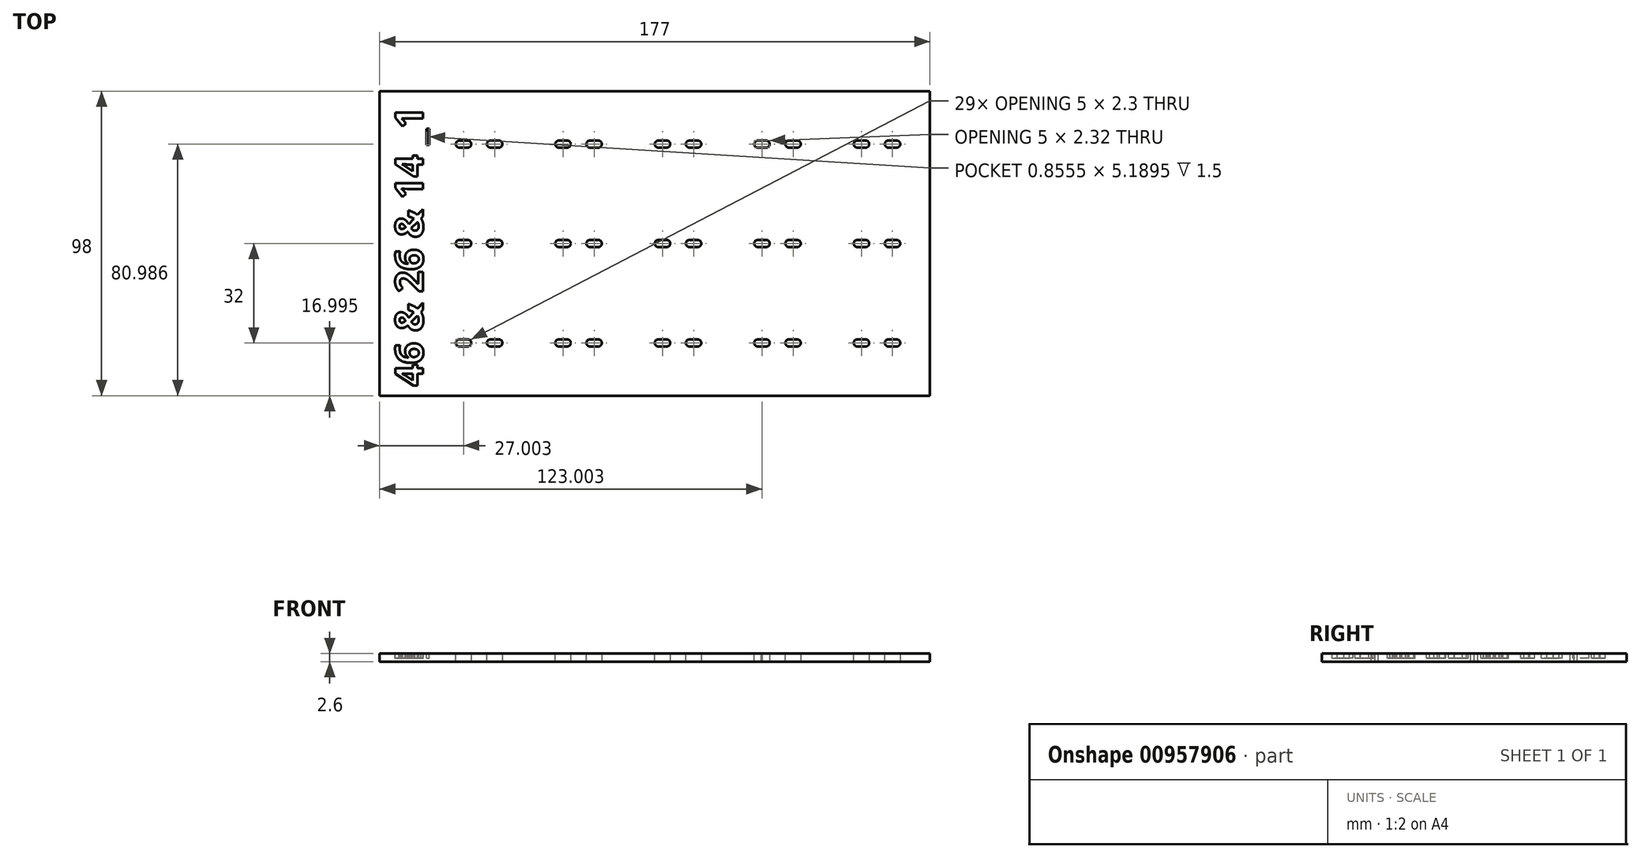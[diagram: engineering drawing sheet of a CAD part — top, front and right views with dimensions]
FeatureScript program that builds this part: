
annotation { "Feature Type Name" : "Feature", "Feature Type Description" : "" }
export const myFeature = defineFeature(function(context is Context, id is Id, definition is map)
    precondition{}
    {
        {
            var Q0;
            Q0=qCreatedBy(makeId("Top.planeOp"),FACE);
            var sketch = newSketch(context, id + "F0", { "sketchPlane" : qUnion([Q0])});
            skLineSegment(sketch, "E0.bottom", {"start": v(-87.55, 48.72) * mm, "end": v(89.45, 48.72) * mm});
            skLineSegment(sketch, "E0.top", {"start": v(-87.55, -49.28) * mm, "end": v(89.45, -49.28) * mm});
            skLineSegment(sketch, "E0.left", {"start": v(-87.55, 48.72) * mm, "end": v(-87.55, -49.28) * mm});
            skLineSegment(sketch, "E0.right", {"start": v(89.45, 48.72) * mm, "end": v(89.45, -49.28) * mm});
            skSolve(sketch);
        }
        {
            var Q0;
            Q0=makeQuery(id+"F0.imprint","IMPRINT",FACE,{"disambiguationData":[TD([[makeQuery(id+"F0.imprint","IMPRINT",EDGE,{"derivedFrom":sQuery(id+"F0.wireOp",EDGE,"E0.bottom")}),-1.0]])]});
            extrude(context, id + "F1", {"entities" : qUnion([Q0]), "depth" : 2.6 * mm, "offsetDistance" : 25 * mm});
        }
        {
            var Q0;
            Q0=makeQuery(id+"F1.opExtrude","CAP_FACE",FACE,{"disambiguationData":[OSD([sQuery(id+"F0.wireOp",EDGE,"E0.bottom"),sQuery(id+"F0.wireOp",EDGE,"E0.top"),sQuery(id+"F0.wireOp",EDGE,"E0.left"),sQuery(id+"F0.wireOp",EDGE,"E0.right")])],"isStart":false});
            var sketch = newSketch(context, id + "F2", { "sketchPlane" : qUnion([Q0])});
            skText(sketch, "E1", { "text": "46 & 26 & 14 _1", "fontName": "OpenSans-Bold.ttf"});
            const initialGuessF2  = {"E1": [-0.07355, -0.04628, 0, 1, 0.009]};
            skSetInitialGuess(sketch, initialGuessF2);
            skSolve(sketch);
        }
        {
            var Q0;
            Q0=qSketchRegion(id+"F2",true);
            extrude(context, id + "F3", {"entities" : qUnion([Q0]), "operationType" : NewBodyOperationType.REMOVE, "oppositeDirection" : true, "depth" : 1.5 * mm, "offsetDistance" : 25 * mm});
        }
        {
            var Q0;
            {var subQ0=sQuery(id+"F0.wireOp",EDGE,"E0.left");var subQ1=sQuery(id+"F0.wireOp",EDGE,"E0.bottom");var subQ2=sQuery(id+"F0.wireOp",EDGE,"E0.right");var subQ3=sQuery(id+"F0.wireOp",EDGE,"E0.top");Q0=makeQuery(id+"F3.boolean.opBoolean","SPLIT",FACE,{"disambiguationData":[TD([makeQuery(id+"F1.opExtrude","SWEPT_FACE",FACE,{"disambiguationData":[OSD([subQ1])]})])],"derivedFrom":makeQuery(id+"F1.opExtrude","CAP_FACE",FACE,{"disambiguationData":[OSD([subQ1,subQ3,subQ0,subQ2])],"isStart":false})});}
            var sketch = newSketch(context, id + "F4", { "sketchPlane" : qUnion([Q0])});
            skCircle(sketch, "E2", {"center": v(-60.55, 31.72) * mm, "radius": 1.15 * mm});
            skCircle(sketch, "E3", {"center": v(-50.55, 31.72) * mm, "radius": 1.15 * mm});
            skCircle(sketch, "E4", {"center": v(-28.55, 31.72) * mm, "radius": 1.15 * mm});
            skCircle(sketch, "E5", {"center": v(-18.55, 31.72) * mm, "radius": 1.15 * mm});
            skCircle(sketch, "E6", {"center": v(3.45, 31.72) * mm, "radius": 1.15 * mm});
            skCircle(sketch, "E7", {"center": v(13.45, 31.72) * mm, "radius": 1.15 * mm});
            skCircle(sketch, "E8", {"center": v(35.45, 31.72) * mm, "radius": 1.15 * mm});
            skCircle(sketch, "E9", {"center": v(45.45, 31.72) * mm, "radius": 1.15 * mm});
            skCircle(sketch, "E10", {"center": v(67.45, 31.72) * mm, "radius": 1.15 * mm});
            skCircle(sketch, "E11", {"center": v(77.45, 31.72) * mm, "radius": 1.15 * mm});
            skCircle(sketch, "E12", {"center": v(-60.55, -0.28) * mm, "radius": 1.15 * mm});
            skCircle(sketch, "E13", {"center": v(-50.55, -0.28) * mm, "radius": 1.15 * mm});
            skCircle(sketch, "E14", {"center": v(-28.55, -0.28) * mm, "radius": 1.15 * mm});
            skCircle(sketch, "E15", {"center": v(-18.55, -0.28) * mm, "radius": 1.15 * mm});
            skCircle(sketch, "E16", {"center": v(3.45, -0.28) * mm, "radius": 1.15 * mm});
            skCircle(sketch, "E17", {"center": v(13.45, -0.28) * mm, "radius": 1.15 * mm});
            skCircle(sketch, "E18", {"center": v(35.45, -0.28) * mm, "radius": 1.15 * mm});
            skCircle(sketch, "E19", {"center": v(45.45, -0.28) * mm, "radius": 1.15 * mm});
            skCircle(sketch, "E20", {"center": v(67.45, -0.28) * mm, "radius": 1.15 * mm});
            skCircle(sketch, "E21", {"center": v(77.45, -0.28) * mm, "radius": 1.15 * mm});
            skCircle(sketch, "E22", {"center": v(-60.55, -32.28) * mm, "radius": 1.15 * mm});
            skCircle(sketch, "E23", {"center": v(-50.55, -32.28) * mm, "radius": 1.15 * mm});
            skCircle(sketch, "E24", {"center": v(-28.55, -32.28) * mm, "radius": 1.15 * mm});
            skCircle(sketch, "E25", {"center": v(-18.55, -32.28) * mm, "radius": 1.15 * mm});
            skCircle(sketch, "E26", {"center": v(3.45, -32.28) * mm, "radius": 1.15 * mm});
            skCircle(sketch, "E27", {"center": v(13.45, -32.28) * mm, "radius": 1.15 * mm});
            skCircle(sketch, "E28", {"center": v(35.45, -32.28) * mm, "radius": 1.15 * mm});
            skCircle(sketch, "E29", {"center": v(45.45, -32.28) * mm, "radius": 1.15 * mm});
            skCircle(sketch, "E30", {"center": v(67.45, -32.28) * mm, "radius": 1.15 * mm});
            skCircle(sketch, "E31", {"center": v(77.45, -32.28) * mm, "radius": 1.15 * mm});
            skLineSegment(sketch, "E32.bottom", {"start": v(-53.05, 32.87) * mm, "end": v(-48.05, 32.87) * mm});
            skLineSegment(sketch, "E32.top", {"start": v(-53.05, 30.57) * mm, "end": v(-48.05, 30.57) * mm});
            skLineSegment(sketch, "E32.left", {"start": v(-53.05, 32.87) * mm, "end": v(-53.05, 30.57) * mm});
            skLineSegment(sketch, "E32.right", {"start": v(-48.05, 32.87) * mm, "end": v(-48.05, 30.57) * mm});
            skLineSegment(sketch, "E33.bottom", {"start": v(-63.05, 32.87) * mm, "end": v(-58.05, 32.87) * mm});
            skLineSegment(sketch, "E33.top", {"start": v(-63.05, 30.57) * mm, "end": v(-58.05, 30.57) * mm});
            skLineSegment(sketch, "E33.left", {"start": v(-63.05, 32.87) * mm, "end": v(-63.05, 30.57) * mm});
            skLineSegment(sketch, "E33.right", {"start": v(-58.05, 32.87) * mm, "end": v(-58.05, 30.57) * mm});
            skLineSegment(sketch, "E34.bottom", {"start": v(-31.05, 32.87) * mm, "end": v(-26.05, 32.87) * mm});
            skLineSegment(sketch, "E34.top", {"start": v(-31.05, 30.57) * mm, "end": v(-26.05, 30.57) * mm});
            skLineSegment(sketch, "E34.left", {"start": v(-31.05, 32.87) * mm, "end": v(-31.05, 30.57) * mm});
            skLineSegment(sketch, "E34.right", {"start": v(-26.05, 32.87) * mm, "end": v(-26.05, 30.57) * mm});
            skLineSegment(sketch, "E35.bottom", {"start": v(-21.05, 32.87) * mm, "end": v(-16.05, 32.87) * mm});
            skLineSegment(sketch, "E35.top", {"start": v(-21.05, 30.57) * mm, "end": v(-16.05, 30.57) * mm});
            skLineSegment(sketch, "E35.left", {"start": v(-21.05, 32.87) * mm, "end": v(-21.05, 30.57) * mm});
            skLineSegment(sketch, "E35.right", {"start": v(-16.05, 32.87) * mm, "end": v(-16.05, 30.57) * mm});
            skLineSegment(sketch, "E36.bottom", {"start": v(0.95, 32.87) * mm, "end": v(5.95, 32.87) * mm});
            skLineSegment(sketch, "E36.top", {"start": v(0.95, 30.57) * mm, "end": v(5.95, 30.57) * mm});
            skLineSegment(sketch, "E36.left", {"start": v(0.95, 32.87) * mm, "end": v(0.95, 30.57) * mm});
            skLineSegment(sketch, "E36.right", {"start": v(5.95, 32.87) * mm, "end": v(5.95, 30.57) * mm});
            skLineSegment(sketch, "E37.bottom", {"start": v(10.95, 32.87) * mm, "end": v(15.95, 32.87) * mm});
            skLineSegment(sketch, "E37.top", {"start": v(10.95, 30.57) * mm, "end": v(15.95, 30.57) * mm});
            skLineSegment(sketch, "E37.left", {"start": v(10.95, 32.87) * mm, "end": v(10.95, 30.57) * mm});
            skLineSegment(sketch, "E37.right", {"start": v(15.95, 32.87) * mm, "end": v(15.95, 30.57) * mm});
            skLineSegment(sketch, "E38.bottom", {"start": v(32.95, 32.85) * mm, "end": v(37.95, 32.85) * mm});
            skLineSegment(sketch, "E38.top", {"start": v(32.95, 30.55) * mm, "end": v(37.95, 30.55) * mm});
            skLineSegment(sketch, "E38.left", {"start": v(32.95, 32.85) * mm, "end": v(32.95, 30.55) * mm});
            skLineSegment(sketch, "E38.right", {"start": v(37.95, 32.85) * mm, "end": v(37.95, 30.55) * mm});
            skLineSegment(sketch, "E39.bottom", {"start": v(42.95, 32.87) * mm, "end": v(47.95, 32.87) * mm});
            skLineSegment(sketch, "E39.top", {"start": v(42.95, 30.57) * mm, "end": v(47.95, 30.57) * mm});
            skLineSegment(sketch, "E39.left", {"start": v(42.95, 32.87) * mm, "end": v(42.95, 30.57) * mm});
            skLineSegment(sketch, "E39.right", {"start": v(47.95, 32.87) * mm, "end": v(47.95, 30.57) * mm});
            skLineSegment(sketch, "E40.bottom", {"start": v(64.95, 32.87) * mm, "end": v(69.95, 32.87) * mm});
            skLineSegment(sketch, "E40.top", {"start": v(64.95, 30.57) * mm, "end": v(69.95, 30.57) * mm});
            skLineSegment(sketch, "E40.left", {"start": v(64.95, 32.87) * mm, "end": v(64.95, 30.57) * mm});
            skLineSegment(sketch, "E40.right", {"start": v(69.95, 32.87) * mm, "end": v(69.95, 30.57) * mm});
            skLineSegment(sketch, "E41.bottom", {"start": v(74.95, 32.87) * mm, "end": v(79.95, 32.87) * mm});
            skLineSegment(sketch, "E41.top", {"start": v(74.95, 30.57) * mm, "end": v(79.95, 30.57) * mm});
            skLineSegment(sketch, "E41.left", {"start": v(74.95, 32.87) * mm, "end": v(74.95, 30.57) * mm});
            skLineSegment(sketch, "E41.right", {"start": v(79.95, 32.87) * mm, "end": v(79.95, 30.57) * mm});
            skLineSegment(sketch, "E42.bottom", {"start": v(74.95, 0.87) * mm, "end": v(79.95, 0.87) * mm});
            skLineSegment(sketch, "E42.top", {"start": v(74.95, -1.43) * mm, "end": v(79.95, -1.43) * mm});
            skLineSegment(sketch, "E42.left", {"start": v(74.95, 0.87) * mm, "end": v(74.95, -1.43) * mm});
            skLineSegment(sketch, "E42.right", {"start": v(79.95, 0.87) * mm, "end": v(79.95, -1.43) * mm});
            skLineSegment(sketch, "E43.bottom", {"start": v(64.95, 0.87) * mm, "end": v(69.95, 0.87) * mm});
            skLineSegment(sketch, "E43.top", {"start": v(64.95, -1.43) * mm, "end": v(69.95, -1.43) * mm});
            skLineSegment(sketch, "E43.left", {"start": v(64.95, 0.87) * mm, "end": v(64.95, -1.43) * mm});
            skLineSegment(sketch, "E43.right", {"start": v(69.95, 0.87) * mm, "end": v(69.95, -1.43) * mm});
            skLineSegment(sketch, "E44.bottom", {"start": v(42.95, 0.87) * mm, "end": v(47.95, 0.87) * mm});
            skLineSegment(sketch, "E44.top", {"start": v(42.95, -1.43) * mm, "end": v(47.95, -1.43) * mm});
            skLineSegment(sketch, "E44.left", {"start": v(42.95, 0.87) * mm, "end": v(42.95, -1.43) * mm});
            skLineSegment(sketch, "E44.right", {"start": v(47.95, 0.87) * mm, "end": v(47.95, -1.43) * mm});
            skLineSegment(sketch, "E45.bottom", {"start": v(32.95, 0.87) * mm, "end": v(37.95, 0.87) * mm});
            skLineSegment(sketch, "E45.top", {"start": v(32.95, -1.43) * mm, "end": v(37.95, -1.43) * mm});
            skLineSegment(sketch, "E45.left", {"start": v(32.95, 0.87) * mm, "end": v(32.95, -1.43) * mm});
            skLineSegment(sketch, "E45.right", {"start": v(37.95, 0.87) * mm, "end": v(37.95, -1.43) * mm});
            skLineSegment(sketch, "E46.bottom", {"start": v(10.95, 0.87) * mm, "end": v(15.95, 0.87) * mm});
            skLineSegment(sketch, "E46.top", {"start": v(10.95, -1.43) * mm, "end": v(15.95, -1.43) * mm});
            skLineSegment(sketch, "E46.left", {"start": v(10.95, 0.87) * mm, "end": v(10.95, -1.43) * mm});
            skLineSegment(sketch, "E46.right", {"start": v(15.95, 0.87) * mm, "end": v(15.95, -1.43) * mm});
            skLineSegment(sketch, "E47.bottom", {"start": v(-63.05, 0.87) * mm, "end": v(-58.05, 0.87) * mm});
            skLineSegment(sketch, "E47.top", {"start": v(-63.05, -1.43) * mm, "end": v(-58.05, -1.43) * mm});
            skLineSegment(sketch, "E47.left", {"start": v(-63.05, 0.87) * mm, "end": v(-63.05, -1.43) * mm});
            skLineSegment(sketch, "E47.right", {"start": v(-58.05, 0.87) * mm, "end": v(-58.05, -1.43) * mm});
            skLineSegment(sketch, "E48.bottom", {"start": v(-53.05, 0.87) * mm, "end": v(-48.05, 0.87) * mm});
            skLineSegment(sketch, "E48.top", {"start": v(-53.05, -1.43) * mm, "end": v(-48.05, -1.43) * mm});
            skLineSegment(sketch, "E48.left", {"start": v(-53.05, 0.87) * mm, "end": v(-53.05, -1.43) * mm});
            skLineSegment(sketch, "E48.right", {"start": v(-48.05, 0.87) * mm, "end": v(-48.05, -1.43) * mm});
            skLineSegment(sketch, "E49.bottom", {"start": v(-31.05, 0.87) * mm, "end": v(-26.05, 0.87) * mm});
            skLineSegment(sketch, "E49.top", {"start": v(-31.05, -1.43) * mm, "end": v(-26.05, -1.43) * mm});
            skLineSegment(sketch, "E49.left", {"start": v(-31.05, 0.87) * mm, "end": v(-31.05, -1.43) * mm});
            skLineSegment(sketch, "E49.right", {"start": v(-26.05, 0.87) * mm, "end": v(-26.05, -1.43) * mm});
            skLineSegment(sketch, "E50.bottom", {"start": v(-21.05, 0.87) * mm, "end": v(-16.05, 0.87) * mm});
            skLineSegment(sketch, "E50.top", {"start": v(-21.05, -1.43) * mm, "end": v(-16.05, -1.43) * mm});
            skLineSegment(sketch, "E50.left", {"start": v(-21.05, 0.87) * mm, "end": v(-21.05, -1.43) * mm});
            skLineSegment(sketch, "E50.right", {"start": v(-16.05, 0.87) * mm, "end": v(-16.05, -1.43) * mm});
            skLineSegment(sketch, "E51.bottom", {"start": v(0.95, 0.87) * mm, "end": v(5.95, 0.87) * mm});
            skLineSegment(sketch, "E51.top", {"start": v(0.95, -1.43) * mm, "end": v(5.95, -1.43) * mm});
            skLineSegment(sketch, "E51.left", {"start": v(0.95, 0.87) * mm, "end": v(0.95, -1.43) * mm});
            skLineSegment(sketch, "E51.right", {"start": v(5.95, 0.87) * mm, "end": v(5.95, -1.43) * mm});
            skLineSegment(sketch, "E52.bottom", {"start": v(-63.05, -31.13) * mm, "end": v(-58.05, -31.13) * mm});
            skLineSegment(sketch, "E52.top", {"start": v(-63.05, -33.43) * mm, "end": v(-58.05, -33.43) * mm});
            skLineSegment(sketch, "E52.left", {"start": v(-63.05, -31.13) * mm, "end": v(-63.05, -33.43) * mm});
            skLineSegment(sketch, "E52.right", {"start": v(-58.05, -31.13) * mm, "end": v(-58.05, -33.43) * mm});
            skLineSegment(sketch, "E53.bottom", {"start": v(-53.05, -31.13) * mm, "end": v(-48.05, -31.13) * mm});
            skLineSegment(sketch, "E53.top", {"start": v(-53.05, -33.43) * mm, "end": v(-48.05, -33.43) * mm});
            skLineSegment(sketch, "E53.left", {"start": v(-53.05, -31.13) * mm, "end": v(-53.05, -33.43) * mm});
            skLineSegment(sketch, "E53.right", {"start": v(-48.05, -31.13) * mm, "end": v(-48.05, -33.43) * mm});
            skLineSegment(sketch, "E54.bottom", {"start": v(-31.05, -31.13) * mm, "end": v(-26.05, -31.13) * mm});
            skLineSegment(sketch, "E54.top", {"start": v(-31.05, -33.43) * mm, "end": v(-26.05, -33.43) * mm});
            skLineSegment(sketch, "E54.left", {"start": v(-31.05, -31.13) * mm, "end": v(-31.05, -33.43) * mm});
            skLineSegment(sketch, "E54.right", {"start": v(-26.05, -31.13) * mm, "end": v(-26.05, -33.43) * mm});
            skLineSegment(sketch, "E55.bottom", {"start": v(-21.05, -31.13) * mm, "end": v(-16.05, -31.13) * mm});
            skLineSegment(sketch, "E55.top", {"start": v(-21.05, -33.43) * mm, "end": v(-16.05, -33.43) * mm});
            skLineSegment(sketch, "E55.left", {"start": v(-21.05, -31.13) * mm, "end": v(-21.05, -33.43) * mm});
            skLineSegment(sketch, "E55.right", {"start": v(-16.05, -31.13) * mm, "end": v(-16.05, -33.43) * mm});
            skLineSegment(sketch, "E56.bottom", {"start": v(0.95, -31.13) * mm, "end": v(5.95, -31.13) * mm});
            skLineSegment(sketch, "E56.top", {"start": v(0.95, -33.43) * mm, "end": v(5.95, -33.43) * mm});
            skLineSegment(sketch, "E56.left", {"start": v(0.95, -31.13) * mm, "end": v(0.95, -33.43) * mm});
            skLineSegment(sketch, "E56.right", {"start": v(5.95, -31.13) * mm, "end": v(5.95, -33.43) * mm});
            skLineSegment(sketch, "E57.bottom", {"start": v(10.95, -31.13) * mm, "end": v(15.95, -31.13) * mm});
            skLineSegment(sketch, "E57.top", {"start": v(10.95, -33.43) * mm, "end": v(15.95, -33.43) * mm});
            skLineSegment(sketch, "E57.left", {"start": v(10.95, -31.13) * mm, "end": v(10.95, -33.43) * mm});
            skLineSegment(sketch, "E57.right", {"start": v(15.95, -31.13) * mm, "end": v(15.95, -33.43) * mm});
            skLineSegment(sketch, "E58.bottom", {"start": v(32.95, -31.13) * mm, "end": v(37.95, -31.13) * mm});
            skLineSegment(sketch, "E58.top", {"start": v(32.95, -33.43) * mm, "end": v(37.95, -33.43) * mm});
            skLineSegment(sketch, "E58.left", {"start": v(32.95, -31.13) * mm, "end": v(32.95, -33.43) * mm});
            skLineSegment(sketch, "E58.right", {"start": v(37.95, -31.13) * mm, "end": v(37.95, -33.43) * mm});
            skLineSegment(sketch, "E59.bottom", {"start": v(42.95, -31.13) * mm, "end": v(47.95, -31.13) * mm});
            skLineSegment(sketch, "E59.top", {"start": v(42.95, -33.43) * mm, "end": v(47.95, -33.43) * mm});
            skLineSegment(sketch, "E59.left", {"start": v(42.95, -31.13) * mm, "end": v(42.95, -33.43) * mm});
            skLineSegment(sketch, "E59.right", {"start": v(47.95, -31.13) * mm, "end": v(47.95, -33.43) * mm});
            skLineSegment(sketch, "E60.bottom", {"start": v(64.95, -31.13) * mm, "end": v(69.95, -31.13) * mm});
            skLineSegment(sketch, "E60.top", {"start": v(64.95, -33.43) * mm, "end": v(69.95, -33.43) * mm});
            skLineSegment(sketch, "E60.left", {"start": v(64.95, -31.13) * mm, "end": v(64.95, -33.43) * mm});
            skLineSegment(sketch, "E60.right", {"start": v(69.95, -31.13) * mm, "end": v(69.95, -33.43) * mm});
            skLineSegment(sketch, "E61.bottom", {"start": v(74.95, -31.13) * mm, "end": v(79.95, -31.13) * mm});
            skLineSegment(sketch, "E61.top", {"start": v(74.95, -33.43) * mm, "end": v(79.95, -33.43) * mm});
            skLineSegment(sketch, "E61.left", {"start": v(74.95, -31.13) * mm, "end": v(74.95, -33.43) * mm});
            skLineSegment(sketch, "E61.right", {"start": v(79.95, -31.13) * mm, "end": v(79.95, -33.43) * mm});
            skSolve(sketch);
        }
        {
            var Q0;
            Q0 = qSketchRegion(id + "F4", true);
            extrude(context, id + "F5", {"entities" : qUnion([Q0]), "operationType" : NewBodyOperationType.REMOVE, "endBound" : BoundingType.UP_TO_NEXT, "oppositeDirection" : true, "depth" : 25 * mm, "offsetDistance" : 25 * mm});
        }
        {
            var Q0;
            Q0=makeQuery(id+"F5.boolean.opBoolean","COPY",EDGE,{"derivedFrom":makeQuery(id+"F5.opExtrude","SWEPT_EDGE",EDGE,{"disambiguationData":[OSD([sQuery(id+"F4.wireOp",EDGE,"E32.bottom"),sQuery(id+"F4.wireOp",EDGE,"E32.left")])]})});
            var Q1;
            Q1=makeQuery(id+"F5.boolean.opBoolean","COPY",EDGE,{"derivedFrom":makeQuery(id+"F5.opExtrude","SWEPT_EDGE",EDGE,{"disambiguationData":[OSD([sQuery(id+"F4.wireOp",EDGE,"E32.bottom"),sQuery(id+"F4.wireOp",EDGE,"E32.right")])]})});
            var Q2;
            Q2=makeQuery(id+"F5.boolean.opBoolean","COPY",EDGE,{"derivedFrom":makeQuery(id+"F5.opExtrude","SWEPT_EDGE",EDGE,{"disambiguationData":[OSD([sQuery(id+"F4.wireOp",EDGE,"E32.top"),sQuery(id+"F4.wireOp",EDGE,"E32.right")])]})});
            var Q3;
            Q3=makeQuery(id+"F5.boolean.opBoolean","COPY",EDGE,{"derivedFrom":makeQuery(id+"F5.opExtrude","SWEPT_EDGE",EDGE,{"disambiguationData":[OSD([sQuery(id+"F4.wireOp",EDGE,"E32.top"),sQuery(id+"F4.wireOp",EDGE,"E32.left")])]})});
            var Q4;
            Q4=makeQuery(id+"F5.boolean.opBoolean","COPY",EDGE,{"derivedFrom":makeQuery(id+"F5.opExtrude","SWEPT_EDGE",EDGE,{"disambiguationData":[OSD([sQuery(id+"F4.wireOp",EDGE,"E33.bottom"),sQuery(id+"F4.wireOp",EDGE,"E33.left")])]})});
            var Q5;
            Q5=makeQuery(id+"F5.boolean.opBoolean","COPY",EDGE,{"derivedFrom":makeQuery(id+"F5.opExtrude","SWEPT_EDGE",EDGE,{"disambiguationData":[OSD([sQuery(id+"F4.wireOp",EDGE,"E47.bottom"),sQuery(id+"F4.wireOp",EDGE,"E47.left")])]})});
            var Q6;
            Q6=makeQuery(id+"F5.boolean.opBoolean","COPY",EDGE,{"derivedFrom":makeQuery(id+"F5.opExtrude","SWEPT_EDGE",EDGE,{"disambiguationData":[OSD([sQuery(id+"F4.wireOp",EDGE,"E48.bottom"),sQuery(id+"F4.wireOp",EDGE,"E48.left")])]})});
            var Q7;
            Q7=makeQuery(id+"F5.boolean.opBoolean","COPY",EDGE,{"derivedFrom":makeQuery(id+"F5.opExtrude","SWEPT_EDGE",EDGE,{"disambiguationData":[OSD([sQuery(id+"F4.wireOp",EDGE,"E49.bottom"),sQuery(id+"F4.wireOp",EDGE,"E49.left")])]})});
            var Q8;
            Q8=makeQuery(id+"F5.boolean.opBoolean","COPY",EDGE,{"derivedFrom":makeQuery(id+"F5.opExtrude","SWEPT_EDGE",EDGE,{"disambiguationData":[OSD([sQuery(id+"F4.wireOp",EDGE,"E50.bottom"),sQuery(id+"F4.wireOp",EDGE,"E50.left")])]})});
            var Q9;
            Q9=makeQuery(id+"F5.boolean.opBoolean","COPY",EDGE,{"derivedFrom":makeQuery(id+"F5.opExtrude","SWEPT_EDGE",EDGE,{"disambiguationData":[OSD([sQuery(id+"F4.wireOp",EDGE,"E34.bottom"),sQuery(id+"F4.wireOp",EDGE,"E34.left")])]})});
            var Q10;
            Q10=makeQuery(id+"F5.boolean.opBoolean","COPY",EDGE,{"derivedFrom":makeQuery(id+"F5.opExtrude","SWEPT_EDGE",EDGE,{"disambiguationData":[OSD([sQuery(id+"F4.wireOp",EDGE,"E35.bottom"),sQuery(id+"F4.wireOp",EDGE,"E35.left")])]})});
            var Q11;
            Q11=makeQuery(id+"F5.boolean.opBoolean","COPY",EDGE,{"derivedFrom":makeQuery(id+"F5.opExtrude","SWEPT_EDGE",EDGE,{"disambiguationData":[OSD([sQuery(id+"F4.wireOp",EDGE,"E52.bottom"),sQuery(id+"F4.wireOp",EDGE,"E52.left")])]})});
            var Q12;
            Q12=makeQuery(id+"F5.boolean.opBoolean","COPY",EDGE,{"derivedFrom":makeQuery(id+"F5.opExtrude","SWEPT_EDGE",EDGE,{"disambiguationData":[OSD([sQuery(id+"F4.wireOp",EDGE,"E53.bottom"),sQuery(id+"F4.wireOp",EDGE,"E53.left")])]})});
            var Q13;
            Q13=makeQuery(id+"F5.boolean.opBoolean","COPY",EDGE,{"derivedFrom":makeQuery(id+"F5.opExtrude","SWEPT_EDGE",EDGE,{"disambiguationData":[OSD([sQuery(id+"F4.wireOp",EDGE,"E54.bottom"),sQuery(id+"F4.wireOp",EDGE,"E54.left")])]})});
            var Q14;
            Q14=makeQuery(id+"F5.boolean.opBoolean","COPY",EDGE,{"derivedFrom":makeQuery(id+"F5.opExtrude","SWEPT_EDGE",EDGE,{"disambiguationData":[OSD([sQuery(id+"F4.wireOp",EDGE,"E55.bottom"),sQuery(id+"F4.wireOp",EDGE,"E55.left")])]})});
            var Q15;
            Q15=makeQuery(id+"F5.boolean.opBoolean","COPY",EDGE,{"derivedFrom":makeQuery(id+"F5.opExtrude","SWEPT_EDGE",EDGE,{"disambiguationData":[OSD([sQuery(id+"F4.wireOp",EDGE,"E56.bottom"),sQuery(id+"F4.wireOp",EDGE,"E56.left")])]})});
            var Q16;
            Q16=makeQuery(id+"F5.boolean.opBoolean","COPY",EDGE,{"derivedFrom":makeQuery(id+"F5.opExtrude","SWEPT_EDGE",EDGE,{"disambiguationData":[OSD([sQuery(id+"F4.wireOp",EDGE,"E57.bottom"),sQuery(id+"F4.wireOp",EDGE,"E57.left")])]})});
            var Q17;
            Q17=makeQuery(id+"F5.boolean.opBoolean","COPY",EDGE,{"derivedFrom":makeQuery(id+"F5.opExtrude","SWEPT_EDGE",EDGE,{"disambiguationData":[OSD([sQuery(id+"F4.wireOp",EDGE,"E36.bottom"),sQuery(id+"F4.wireOp",EDGE,"E36.left")])]})});
            var Q18;
            Q18=makeQuery(id+"F5.boolean.opBoolean","COPY",EDGE,{"derivedFrom":makeQuery(id+"F5.opExtrude","SWEPT_EDGE",EDGE,{"disambiguationData":[OSD([sQuery(id+"F4.wireOp",EDGE,"E37.bottom"),sQuery(id+"F4.wireOp",EDGE,"E37.left")])]})});
            var Q19;
            Q19=makeQuery(id+"F5.boolean.opBoolean","COPY",EDGE,{"derivedFrom":makeQuery(id+"F5.opExtrude","SWEPT_EDGE",EDGE,{"disambiguationData":[OSD([sQuery(id+"F4.wireOp",EDGE,"E38.bottom"),sQuery(id+"F4.wireOp",EDGE,"E38.left")])]})});
            var Q20;
            Q20=makeQuery(id+"F5.boolean.opBoolean","COPY",EDGE,{"derivedFrom":makeQuery(id+"F5.opExtrude","SWEPT_EDGE",EDGE,{"disambiguationData":[OSD([sQuery(id+"F4.wireOp",EDGE,"E39.bottom"),sQuery(id+"F4.wireOp",EDGE,"E39.left")])]})});
            var Q21;
            Q21=makeQuery(id+"F5.boolean.opBoolean","COPY",EDGE,{"derivedFrom":makeQuery(id+"F5.opExtrude","SWEPT_EDGE",EDGE,{"disambiguationData":[OSD([sQuery(id+"F4.wireOp",EDGE,"E40.bottom"),sQuery(id+"F4.wireOp",EDGE,"E40.left")])]})});
            var Q22;
            Q22=makeQuery(id+"F5.boolean.opBoolean","COPY",EDGE,{"derivedFrom":makeQuery(id+"F5.opExtrude","SWEPT_EDGE",EDGE,{"disambiguationData":[OSD([sQuery(id+"F4.wireOp",EDGE,"E41.bottom"),sQuery(id+"F4.wireOp",EDGE,"E41.left")])]})});
            var Q23;
            Q23=makeQuery(id+"F5.boolean.opBoolean","COPY",EDGE,{"derivedFrom":makeQuery(id+"F5.opExtrude","SWEPT_EDGE",EDGE,{"disambiguationData":[OSD([sQuery(id+"F4.wireOp",EDGE,"E60.bottom"),sQuery(id+"F4.wireOp",EDGE,"E60.left")])]})});
            var Q24;
            Q24=makeQuery(id+"F5.boolean.opBoolean","COPY",EDGE,{"derivedFrom":makeQuery(id+"F5.opExtrude","SWEPT_EDGE",EDGE,{"disambiguationData":[OSD([sQuery(id+"F4.wireOp",EDGE,"E59.bottom"),sQuery(id+"F4.wireOp",EDGE,"E59.left")])]})});
            var Q25;
            Q25=makeQuery(id+"F5.boolean.opBoolean","COPY",EDGE,{"derivedFrom":makeQuery(id+"F5.opExtrude","SWEPT_EDGE",EDGE,{"disambiguationData":[OSD([sQuery(id+"F4.wireOp",EDGE,"E58.bottom"),sQuery(id+"F4.wireOp",EDGE,"E58.left")])]})});
            var Q26;
            Q26=makeQuery(id+"F5.boolean.opBoolean","COPY",EDGE,{"derivedFrom":makeQuery(id+"F5.opExtrude","SWEPT_EDGE",EDGE,{"disambiguationData":[OSD([sQuery(id+"F4.wireOp",EDGE,"E51.bottom"),sQuery(id+"F4.wireOp",EDGE,"E51.left")])]})});
            var Q27;
            Q27=makeQuery(id+"F5.boolean.opBoolean","COPY",EDGE,{"derivedFrom":makeQuery(id+"F5.opExtrude","SWEPT_EDGE",EDGE,{"disambiguationData":[OSD([sQuery(id+"F4.wireOp",EDGE,"E46.bottom"),sQuery(id+"F4.wireOp",EDGE,"E46.left")])]})});
            var Q28;
            Q28=makeQuery(id+"F5.boolean.opBoolean","COPY",EDGE,{"derivedFrom":makeQuery(id+"F5.opExtrude","SWEPT_EDGE",EDGE,{"disambiguationData":[OSD([sQuery(id+"F4.wireOp",EDGE,"E45.bottom"),sQuery(id+"F4.wireOp",EDGE,"E45.left")])]})});
            var Q29;
            Q29=makeQuery(id+"F5.boolean.opBoolean","COPY",EDGE,{"derivedFrom":makeQuery(id+"F5.opExtrude","SWEPT_EDGE",EDGE,{"disambiguationData":[OSD([sQuery(id+"F4.wireOp",EDGE,"E44.bottom"),sQuery(id+"F4.wireOp",EDGE,"E44.left")])]})});
            var Q30;
            Q30=makeQuery(id+"F5.boolean.opBoolean","COPY",EDGE,{"derivedFrom":makeQuery(id+"F5.opExtrude","SWEPT_EDGE",EDGE,{"disambiguationData":[OSD([sQuery(id+"F4.wireOp",EDGE,"E43.bottom"),sQuery(id+"F4.wireOp",EDGE,"E43.left")])]})});
            var Q31;
            Q31=makeQuery(id+"F5.boolean.opBoolean","COPY",EDGE,{"derivedFrom":makeQuery(id+"F5.opExtrude","SWEPT_EDGE",EDGE,{"disambiguationData":[OSD([sQuery(id+"F4.wireOp",EDGE,"E42.bottom"),sQuery(id+"F4.wireOp",EDGE,"E42.left")])]})});
            var Q32;
            Q32=makeQuery(id+"F5.boolean.opBoolean","COPY",EDGE,{"derivedFrom":makeQuery(id+"F5.opExtrude","SWEPT_EDGE",EDGE,{"disambiguationData":[OSD([sQuery(id+"F4.wireOp",EDGE,"E61.bottom"),sQuery(id+"F4.wireOp",EDGE,"E61.left")])]})});
            var Q33;
            Q33=makeQuery(id+"F5.boolean.opBoolean","COPY",EDGE,{"derivedFrom":makeQuery(id+"F5.opExtrude","SWEPT_EDGE",EDGE,{"disambiguationData":[OSD([sQuery(id+"F4.wireOp",EDGE,"E33.bottom"),sQuery(id+"F4.wireOp",EDGE,"E33.right")])]})});
            var Q34;
            Q34=makeQuery(id+"F5.boolean.opBoolean","COPY",EDGE,{"derivedFrom":makeQuery(id+"F5.opExtrude","SWEPT_EDGE",EDGE,{"disambiguationData":[OSD([sQuery(id+"F4.wireOp",EDGE,"E34.bottom"),sQuery(id+"F4.wireOp",EDGE,"E34.right")])]})});
            var Q35;
            Q35=makeQuery(id+"F5.boolean.opBoolean","COPY",EDGE,{"derivedFrom":makeQuery(id+"F5.opExtrude","SWEPT_EDGE",EDGE,{"disambiguationData":[OSD([sQuery(id+"F4.wireOp",EDGE,"E35.bottom"),sQuery(id+"F4.wireOp",EDGE,"E35.right")])]})});
            var Q36;
            Q36=makeQuery(id+"F5.boolean.opBoolean","COPY",EDGE,{"derivedFrom":makeQuery(id+"F5.opExtrude","SWEPT_EDGE",EDGE,{"disambiguationData":[OSD([sQuery(id+"F4.wireOp",EDGE,"E50.bottom"),sQuery(id+"F4.wireOp",EDGE,"E50.right")])]})});
            var Q37;
            Q37=makeQuery(id+"F5.boolean.opBoolean","COPY",EDGE,{"derivedFrom":makeQuery(id+"F5.opExtrude","SWEPT_EDGE",EDGE,{"disambiguationData":[OSD([sQuery(id+"F4.wireOp",EDGE,"E48.bottom"),sQuery(id+"F4.wireOp",EDGE,"E48.right")])]})});
            var Q38;
            Q38=makeQuery(id+"F5.boolean.opBoolean","COPY",EDGE,{"derivedFrom":makeQuery(id+"F5.opExtrude","SWEPT_EDGE",EDGE,{"disambiguationData":[OSD([sQuery(id+"F4.wireOp",EDGE,"E47.bottom"),sQuery(id+"F4.wireOp",EDGE,"E47.right")])]})});
            var Q39;
            Q39=makeQuery(id+"F5.boolean.opBoolean","COPY",EDGE,{"derivedFrom":makeQuery(id+"F5.opExtrude","SWEPT_EDGE",EDGE,{"disambiguationData":[OSD([sQuery(id+"F4.wireOp",EDGE,"E52.bottom"),sQuery(id+"F4.wireOp",EDGE,"E52.right")])]})});
            var Q40;
            Q40=makeQuery(id+"F5.boolean.opBoolean","COPY",EDGE,{"derivedFrom":makeQuery(id+"F5.opExtrude","SWEPT_EDGE",EDGE,{"disambiguationData":[OSD([sQuery(id+"F4.wireOp",EDGE,"E53.bottom"),sQuery(id+"F4.wireOp",EDGE,"E53.right")])]})});
            var Q41;
            Q41=makeQuery(id+"F5.boolean.opBoolean","COPY",EDGE,{"derivedFrom":makeQuery(id+"F5.opExtrude","SWEPT_EDGE",EDGE,{"disambiguationData":[OSD([sQuery(id+"F4.wireOp",EDGE,"E54.bottom"),sQuery(id+"F4.wireOp",EDGE,"E54.right")])]})});
            var Q42;
            Q42=makeQuery(id+"F5.boolean.opBoolean","COPY",EDGE,{"derivedFrom":makeQuery(id+"F5.opExtrude","SWEPT_EDGE",EDGE,{"disambiguationData":[OSD([sQuery(id+"F4.wireOp",EDGE,"E55.bottom"),sQuery(id+"F4.wireOp",EDGE,"E55.right")])]})});
            var Q43;
            Q43=makeQuery(id+"F5.boolean.opBoolean","COPY",EDGE,{"derivedFrom":makeQuery(id+"F5.opExtrude","SWEPT_EDGE",EDGE,{"disambiguationData":[OSD([sQuery(id+"F4.wireOp",EDGE,"E51.bottom"),sQuery(id+"F4.wireOp",EDGE,"E51.right")])]})});
            var Q44;
            Q44=makeQuery(id+"F5.boolean.opBoolean","COPY",EDGE,{"derivedFrom":makeQuery(id+"F5.opExtrude","SWEPT_EDGE",EDGE,{"disambiguationData":[OSD([sQuery(id+"F4.wireOp",EDGE,"E46.bottom"),sQuery(id+"F4.wireOp",EDGE,"E46.right")])]})});
            var Q45;
            Q45=makeQuery(id+"F5.boolean.opBoolean","COPY",EDGE,{"derivedFrom":makeQuery(id+"F5.opExtrude","SWEPT_EDGE",EDGE,{"disambiguationData":[OSD([sQuery(id+"F4.wireOp",EDGE,"E36.bottom"),sQuery(id+"F4.wireOp",EDGE,"E36.right")])]})});
            var Q46;
            Q46=makeQuery(id+"F5.boolean.opBoolean","COPY",EDGE,{"derivedFrom":makeQuery(id+"F5.opExtrude","SWEPT_EDGE",EDGE,{"disambiguationData":[OSD([sQuery(id+"F4.wireOp",EDGE,"E37.bottom"),sQuery(id+"F4.wireOp",EDGE,"E37.right")])]})});
            var Q47;
            Q47=makeQuery(id+"F5.boolean.opBoolean","COPY",EDGE,{"derivedFrom":makeQuery(id+"F5.opExtrude","SWEPT_EDGE",EDGE,{"disambiguationData":[OSD([sQuery(id+"F4.wireOp",EDGE,"E38.bottom"),sQuery(id+"F4.wireOp",EDGE,"E38.right")])]})});
            var Q48;
            Q48=makeQuery(id+"F5.boolean.opBoolean","COPY",EDGE,{"derivedFrom":makeQuery(id+"F5.opExtrude","SWEPT_EDGE",EDGE,{"disambiguationData":[OSD([sQuery(id+"F4.wireOp",EDGE,"E39.bottom"),sQuery(id+"F4.wireOp",EDGE,"E39.right")])]})});
            var Q49;
            Q49=makeQuery(id+"F5.boolean.opBoolean","COPY",EDGE,{"derivedFrom":makeQuery(id+"F5.opExtrude","SWEPT_EDGE",EDGE,{"disambiguationData":[OSD([sQuery(id+"F4.wireOp",EDGE,"E56.bottom"),sQuery(id+"F4.wireOp",EDGE,"E56.right")])]})});
            var Q50;
            Q50=makeQuery(id+"F5.boolean.opBoolean","COPY",EDGE,{"derivedFrom":makeQuery(id+"F5.opExtrude","SWEPT_EDGE",EDGE,{"disambiguationData":[OSD([sQuery(id+"F4.wireOp",EDGE,"E57.bottom"),sQuery(id+"F4.wireOp",EDGE,"E57.right")])]})});
            var Q51;
            Q51=makeQuery(id+"F5.boolean.opBoolean","COPY",EDGE,{"derivedFrom":makeQuery(id+"F5.opExtrude","SWEPT_EDGE",EDGE,{"disambiguationData":[OSD([sQuery(id+"F4.wireOp",EDGE,"E58.bottom"),sQuery(id+"F4.wireOp",EDGE,"E58.right")])]})});
            var Q52;
            Q52=makeQuery(id+"F5.boolean.opBoolean","COPY",EDGE,{"derivedFrom":makeQuery(id+"F5.opExtrude","SWEPT_EDGE",EDGE,{"disambiguationData":[OSD([sQuery(id+"F4.wireOp",EDGE,"E59.bottom"),sQuery(id+"F4.wireOp",EDGE,"E59.right")])]})});
            var Q53;
            Q53=makeQuery(id+"F5.boolean.opBoolean","COPY",EDGE,{"derivedFrom":makeQuery(id+"F5.opExtrude","SWEPT_EDGE",EDGE,{"disambiguationData":[OSD([sQuery(id+"F4.wireOp",EDGE,"E60.bottom"),sQuery(id+"F4.wireOp",EDGE,"E60.right")])]})});
            var Q54;
            Q54=makeQuery(id+"F5.boolean.opBoolean","COPY",EDGE,{"derivedFrom":makeQuery(id+"F5.opExtrude","SWEPT_EDGE",EDGE,{"disambiguationData":[OSD([sQuery(id+"F4.wireOp",EDGE,"E61.bottom"),sQuery(id+"F4.wireOp",EDGE,"E61.right")])]})});
            var Q55;
            Q55=makeQuery(id+"F5.boolean.opBoolean","COPY",EDGE,{"derivedFrom":makeQuery(id+"F5.opExtrude","SWEPT_EDGE",EDGE,{"disambiguationData":[OSD([sQuery(id+"F4.wireOp",EDGE,"E45.bottom"),sQuery(id+"F4.wireOp",EDGE,"E45.right")])]})});
            var Q56;
            Q56=makeQuery(id+"F5.boolean.opBoolean","COPY",EDGE,{"derivedFrom":makeQuery(id+"F5.opExtrude","SWEPT_EDGE",EDGE,{"disambiguationData":[OSD([sQuery(id+"F4.wireOp",EDGE,"E44.bottom"),sQuery(id+"F4.wireOp",EDGE,"E44.right")])]})});
            var Q57;
            Q57=makeQuery(id+"F5.boolean.opBoolean","COPY",EDGE,{"derivedFrom":makeQuery(id+"F5.opExtrude","SWEPT_EDGE",EDGE,{"disambiguationData":[OSD([sQuery(id+"F4.wireOp",EDGE,"E43.bottom"),sQuery(id+"F4.wireOp",EDGE,"E43.right")])]})});
            var Q58;
            Q58=makeQuery(id+"F5.boolean.opBoolean","COPY",EDGE,{"derivedFrom":makeQuery(id+"F5.opExtrude","SWEPT_EDGE",EDGE,{"disambiguationData":[OSD([sQuery(id+"F4.wireOp",EDGE,"E42.bottom"),sQuery(id+"F4.wireOp",EDGE,"E42.right")])]})});
            var Q59;
            Q59=makeQuery(id+"F5.boolean.opBoolean","COPY",EDGE,{"derivedFrom":makeQuery(id+"F5.opExtrude","SWEPT_EDGE",EDGE,{"disambiguationData":[OSD([sQuery(id+"F4.wireOp",EDGE,"E41.bottom"),sQuery(id+"F4.wireOp",EDGE,"E41.right")])]})});
            var Q60;
            Q60=makeQuery(id+"F5.boolean.opBoolean","COPY",EDGE,{"derivedFrom":makeQuery(id+"F5.opExtrude","SWEPT_EDGE",EDGE,{"disambiguationData":[OSD([sQuery(id+"F4.wireOp",EDGE,"E40.bottom"),sQuery(id+"F4.wireOp",EDGE,"E40.right")])]})});
            var Q61;
            Q61=makeQuery(id+"F5.boolean.opBoolean","COPY",EDGE,{"derivedFrom":makeQuery(id+"F5.opExtrude","SWEPT_EDGE",EDGE,{"disambiguationData":[OSD([sQuery(id+"F4.wireOp",EDGE,"E61.top"),sQuery(id+"F4.wireOp",EDGE,"E61.left")])]})});
            var Q62;
            Q62=makeQuery(id+"F5.boolean.opBoolean","COPY",EDGE,{"derivedFrom":makeQuery(id+"F5.opExtrude","SWEPT_EDGE",EDGE,{"disambiguationData":[OSD([sQuery(id+"F4.wireOp",EDGE,"E60.top"),sQuery(id+"F4.wireOp",EDGE,"E60.left")])]})});
            var Q63;
            Q63=makeQuery(id+"F5.boolean.opBoolean","COPY",EDGE,{"derivedFrom":makeQuery(id+"F5.opExtrude","SWEPT_EDGE",EDGE,{"disambiguationData":[OSD([sQuery(id+"F4.wireOp",EDGE,"E59.top"),sQuery(id+"F4.wireOp",EDGE,"E59.left")])]})});
            var Q64;
            Q64=makeQuery(id+"F5.boolean.opBoolean","COPY",EDGE,{"derivedFrom":makeQuery(id+"F5.opExtrude","SWEPT_EDGE",EDGE,{"disambiguationData":[OSD([sQuery(id+"F4.wireOp",EDGE,"E58.top"),sQuery(id+"F4.wireOp",EDGE,"E58.left")])]})});
            var Q65;
            Q65=makeQuery(id+"F5.boolean.opBoolean","COPY",EDGE,{"derivedFrom":makeQuery(id+"F5.opExtrude","SWEPT_EDGE",EDGE,{"disambiguationData":[OSD([sQuery(id+"F4.wireOp",EDGE,"E57.top"),sQuery(id+"F4.wireOp",EDGE,"E57.left")])]})});
            var Q66;
            Q66=makeQuery(id+"F5.boolean.opBoolean","COPY",EDGE,{"derivedFrom":makeQuery(id+"F5.opExtrude","SWEPT_EDGE",EDGE,{"disambiguationData":[OSD([sQuery(id+"F4.wireOp",EDGE,"E56.top"),sQuery(id+"F4.wireOp",EDGE,"E56.left")])]})});
            var Q67;
            Q67=makeQuery(id+"F5.boolean.opBoolean","COPY",EDGE,{"derivedFrom":makeQuery(id+"F5.opExtrude","SWEPT_EDGE",EDGE,{"disambiguationData":[OSD([sQuery(id+"F4.wireOp",EDGE,"E55.top"),sQuery(id+"F4.wireOp",EDGE,"E55.left")])]})});
            var Q68;
            Q68=makeQuery(id+"F5.boolean.opBoolean","COPY",EDGE,{"derivedFrom":makeQuery(id+"F5.opExtrude","SWEPT_EDGE",EDGE,{"disambiguationData":[OSD([sQuery(id+"F4.wireOp",EDGE,"E54.top"),sQuery(id+"F4.wireOp",EDGE,"E54.left")])]})});
            var Q69;
            Q69=makeQuery(id+"F5.boolean.opBoolean","COPY",EDGE,{"derivedFrom":makeQuery(id+"F5.opExtrude","SWEPT_EDGE",EDGE,{"disambiguationData":[OSD([sQuery(id+"F4.wireOp",EDGE,"E42.top"),sQuery(id+"F4.wireOp",EDGE,"E42.left")])]})});
            var Q70;
            Q70=makeQuery(id+"F5.boolean.opBoolean","COPY",EDGE,{"derivedFrom":makeQuery(id+"F5.opExtrude","SWEPT_EDGE",EDGE,{"disambiguationData":[OSD([sQuery(id+"F4.wireOp",EDGE,"E43.top"),sQuery(id+"F4.wireOp",EDGE,"E43.left")])]})});
            var Q71;
            Q71=makeQuery(id+"F5.boolean.opBoolean","COPY",EDGE,{"derivedFrom":makeQuery(id+"F5.opExtrude","SWEPT_EDGE",EDGE,{"disambiguationData":[OSD([sQuery(id+"F4.wireOp",EDGE,"E44.top"),sQuery(id+"F4.wireOp",EDGE,"E44.left")])]})});
            var Q72;
            Q72=makeQuery(id+"F5.boolean.opBoolean","COPY",EDGE,{"derivedFrom":makeQuery(id+"F5.opExtrude","SWEPT_EDGE",EDGE,{"disambiguationData":[OSD([sQuery(id+"F4.wireOp",EDGE,"E45.top"),sQuery(id+"F4.wireOp",EDGE,"E45.left")])]})});
            var Q73;
            Q73=makeQuery(id+"F5.boolean.opBoolean","COPY",EDGE,{"derivedFrom":makeQuery(id+"F5.opExtrude","SWEPT_EDGE",EDGE,{"disambiguationData":[OSD([sQuery(id+"F4.wireOp",EDGE,"E46.top"),sQuery(id+"F4.wireOp",EDGE,"E46.left")])]})});
            var Q74;
            Q74=makeQuery(id+"F5.boolean.opBoolean","COPY",EDGE,{"derivedFrom":makeQuery(id+"F5.opExtrude","SWEPT_EDGE",EDGE,{"disambiguationData":[OSD([sQuery(id+"F4.wireOp",EDGE,"E51.top"),sQuery(id+"F4.wireOp",EDGE,"E51.left")])]})});
            var Q75;
            Q75=makeQuery(id+"F5.boolean.opBoolean","COPY",EDGE,{"derivedFrom":makeQuery(id+"F5.opExtrude","SWEPT_EDGE",EDGE,{"disambiguationData":[OSD([sQuery(id+"F4.wireOp",EDGE,"E50.top"),sQuery(id+"F4.wireOp",EDGE,"E50.left")])]})});
            var Q76;
            Q76=makeQuery(id+"F5.boolean.opBoolean","COPY",EDGE,{"derivedFrom":makeQuery(id+"F5.opExtrude","SWEPT_EDGE",EDGE,{"disambiguationData":[OSD([sQuery(id+"F4.wireOp",EDGE,"E49.top"),sQuery(id+"F4.wireOp",EDGE,"E49.left")])]})});
            var Q77;
            Q77=makeQuery(id+"F5.boolean.opBoolean","COPY",EDGE,{"derivedFrom":makeQuery(id+"F5.opExtrude","SWEPT_EDGE",EDGE,{"disambiguationData":[OSD([sQuery(id+"F4.wireOp",EDGE,"E48.top"),sQuery(id+"F4.wireOp",EDGE,"E48.left")])]})});
            var Q78;
            Q78=makeQuery(id+"F5.boolean.opBoolean","COPY",EDGE,{"derivedFrom":makeQuery(id+"F5.opExtrude","SWEPT_EDGE",EDGE,{"disambiguationData":[OSD([sQuery(id+"F4.wireOp",EDGE,"E34.top"),sQuery(id+"F4.wireOp",EDGE,"E34.left")])]})});
            var Q79;
            Q79=makeQuery(id+"F5.boolean.opBoolean","COPY",EDGE,{"derivedFrom":makeQuery(id+"F5.opExtrude","SWEPT_EDGE",EDGE,{"disambiguationData":[OSD([sQuery(id+"F4.wireOp",EDGE,"E35.top"),sQuery(id+"F4.wireOp",EDGE,"E35.left")])]})});
            var Q80;
            Q80=makeQuery(id+"F5.boolean.opBoolean","COPY",EDGE,{"derivedFrom":makeQuery(id+"F5.opExtrude","SWEPT_EDGE",EDGE,{"disambiguationData":[OSD([sQuery(id+"F4.wireOp",EDGE,"E36.top"),sQuery(id+"F4.wireOp",EDGE,"E36.left")])]})});
            var Q81;
            Q81=makeQuery(id+"F5.boolean.opBoolean","COPY",EDGE,{"derivedFrom":makeQuery(id+"F5.opExtrude","SWEPT_EDGE",EDGE,{"disambiguationData":[OSD([sQuery(id+"F4.wireOp",EDGE,"E37.top"),sQuery(id+"F4.wireOp",EDGE,"E37.left")])]})});
            var Q82;
            Q82=makeQuery(id+"F5.boolean.opBoolean","COPY",EDGE,{"derivedFrom":makeQuery(id+"F5.opExtrude","SWEPT_EDGE",EDGE,{"disambiguationData":[OSD([sQuery(id+"F4.wireOp",EDGE,"E38.top"),sQuery(id+"F4.wireOp",EDGE,"E38.left")])]})});
            var Q83;
            Q83=makeQuery(id+"F5.boolean.opBoolean","COPY",EDGE,{"derivedFrom":makeQuery(id+"F5.opExtrude","SWEPT_EDGE",EDGE,{"disambiguationData":[OSD([sQuery(id+"F4.wireOp",EDGE,"E39.top"),sQuery(id+"F4.wireOp",EDGE,"E39.left")])]})});
            var Q84;
            Q84=makeQuery(id+"F5.boolean.opBoolean","COPY",EDGE,{"derivedFrom":makeQuery(id+"F5.opExtrude","SWEPT_EDGE",EDGE,{"disambiguationData":[OSD([sQuery(id+"F4.wireOp",EDGE,"E40.top"),sQuery(id+"F4.wireOp",EDGE,"E40.left")])]})});
            var Q85;
            Q85=makeQuery(id+"F5.boolean.opBoolean","COPY",EDGE,{"derivedFrom":makeQuery(id+"F5.opExtrude","SWEPT_EDGE",EDGE,{"disambiguationData":[OSD([sQuery(id+"F4.wireOp",EDGE,"E41.top"),sQuery(id+"F4.wireOp",EDGE,"E41.left")])]})});
            var Q86;
            Q86=makeQuery(id+"F5.boolean.opBoolean","COPY",EDGE,{"derivedFrom":makeQuery(id+"F5.opExtrude","SWEPT_EDGE",EDGE,{"disambiguationData":[OSD([sQuery(id+"F4.wireOp",EDGE,"E53.top"),sQuery(id+"F4.wireOp",EDGE,"E53.left")])]})});
            var Q87;
            Q87=makeQuery(id+"F5.boolean.opBoolean","COPY",EDGE,{"derivedFrom":makeQuery(id+"F5.opExtrude","SWEPT_EDGE",EDGE,{"disambiguationData":[OSD([sQuery(id+"F4.wireOp",EDGE,"E52.top"),sQuery(id+"F4.wireOp",EDGE,"E52.left")])]})});
            var Q88;
            Q88=makeQuery(id+"F5.boolean.opBoolean","COPY",EDGE,{"derivedFrom":makeQuery(id+"F5.opExtrude","SWEPT_EDGE",EDGE,{"disambiguationData":[OSD([sQuery(id+"F4.wireOp",EDGE,"E47.top"),sQuery(id+"F4.wireOp",EDGE,"E47.left")])]})});
            var Q89;
            Q89=makeQuery(id+"F5.boolean.opBoolean","COPY",EDGE,{"derivedFrom":makeQuery(id+"F5.opExtrude","SWEPT_EDGE",EDGE,{"disambiguationData":[OSD([sQuery(id+"F4.wireOp",EDGE,"E33.top"),sQuery(id+"F4.wireOp",EDGE,"E33.left")])]})});
            var Q90;
            Q90=makeQuery(id+"F5.boolean.opBoolean","COPY",EDGE,{"derivedFrom":makeQuery(id+"F5.opExtrude","SWEPT_EDGE",EDGE,{"disambiguationData":[OSD([sQuery(id+"F4.wireOp",EDGE,"E41.top"),sQuery(id+"F4.wireOp",EDGE,"E41.right")])]})});
            var Q91;
            Q91=makeQuery(id+"F5.boolean.opBoolean","COPY",EDGE,{"derivedFrom":makeQuery(id+"F5.opExtrude","SWEPT_EDGE",EDGE,{"disambiguationData":[OSD([sQuery(id+"F4.wireOp",EDGE,"E40.top"),sQuery(id+"F4.wireOp",EDGE,"E40.right")])]})});
            var Q92;
            Q92=makeQuery(id+"F5.boolean.opBoolean","COPY",EDGE,{"derivedFrom":makeQuery(id+"F5.opExtrude","SWEPT_EDGE",EDGE,{"disambiguationData":[OSD([sQuery(id+"F4.wireOp",EDGE,"E39.top"),sQuery(id+"F4.wireOp",EDGE,"E39.right")])]})});
            var Q93;
            Q93=makeQuery(id+"F5.boolean.opBoolean","COPY",EDGE,{"derivedFrom":makeQuery(id+"F5.opExtrude","SWEPT_EDGE",EDGE,{"disambiguationData":[OSD([sQuery(id+"F4.wireOp",EDGE,"E38.top"),sQuery(id+"F4.wireOp",EDGE,"E38.right")])]})});
            var Q94;
            Q94=makeQuery(id+"F5.boolean.opBoolean","COPY",EDGE,{"derivedFrom":makeQuery(id+"F5.opExtrude","SWEPT_EDGE",EDGE,{"disambiguationData":[OSD([sQuery(id+"F4.wireOp",EDGE,"E37.top"),sQuery(id+"F4.wireOp",EDGE,"E37.right")])]})});
            var Q95;
            Q95=makeQuery(id+"F5.boolean.opBoolean","COPY",EDGE,{"derivedFrom":makeQuery(id+"F5.opExtrude","SWEPT_EDGE",EDGE,{"disambiguationData":[OSD([sQuery(id+"F4.wireOp",EDGE,"E36.top"),sQuery(id+"F4.wireOp",EDGE,"E36.right")])]})});
            var Q96;
            Q96=makeQuery(id+"F5.boolean.opBoolean","COPY",EDGE,{"derivedFrom":makeQuery(id+"F5.opExtrude","SWEPT_EDGE",EDGE,{"disambiguationData":[OSD([sQuery(id+"F4.wireOp",EDGE,"E35.top"),sQuery(id+"F4.wireOp",EDGE,"E35.right")])]})});
            var Q97;
            Q97=makeQuery(id+"F5.boolean.opBoolean","COPY",EDGE,{"derivedFrom":makeQuery(id+"F5.opExtrude","SWEPT_EDGE",EDGE,{"disambiguationData":[OSD([sQuery(id+"F4.wireOp",EDGE,"E51.top"),sQuery(id+"F4.wireOp",EDGE,"E51.right")])]})});
            var Q98;
            Q98=makeQuery(id+"F5.boolean.opBoolean","COPY",EDGE,{"derivedFrom":makeQuery(id+"F5.opExtrude","SWEPT_EDGE",EDGE,{"disambiguationData":[OSD([sQuery(id+"F4.wireOp",EDGE,"E46.top"),sQuery(id+"F4.wireOp",EDGE,"E46.right")])]})});
            var Q99;
            Q99=makeQuery(id+"F5.boolean.opBoolean","COPY",EDGE,{"derivedFrom":makeQuery(id+"F5.opExtrude","SWEPT_EDGE",EDGE,{"disambiguationData":[OSD([sQuery(id+"F4.wireOp",EDGE,"E45.top"),sQuery(id+"F4.wireOp",EDGE,"E45.right")])]})});
            var Q100;
            Q100=makeQuery(id+"F5.boolean.opBoolean","COPY",EDGE,{"derivedFrom":makeQuery(id+"F5.opExtrude","SWEPT_EDGE",EDGE,{"disambiguationData":[OSD([sQuery(id+"F4.wireOp",EDGE,"E44.top"),sQuery(id+"F4.wireOp",EDGE,"E44.right")])]})});
            var Q101;
            Q101=makeQuery(id+"F5.boolean.opBoolean","COPY",EDGE,{"derivedFrom":makeQuery(id+"F5.opExtrude","SWEPT_EDGE",EDGE,{"disambiguationData":[OSD([sQuery(id+"F4.wireOp",EDGE,"E43.top"),sQuery(id+"F4.wireOp",EDGE,"E43.right")])]})});
            var Q102;
            Q102=makeQuery(id+"F5.boolean.opBoolean","COPY",EDGE,{"derivedFrom":makeQuery(id+"F5.opExtrude","SWEPT_EDGE",EDGE,{"disambiguationData":[OSD([sQuery(id+"F4.wireOp",EDGE,"E42.top"),sQuery(id+"F4.wireOp",EDGE,"E42.right")])]})});
            var Q103;
            Q103=makeQuery(id+"F5.boolean.opBoolean","COPY",EDGE,{"derivedFrom":makeQuery(id+"F5.opExtrude","SWEPT_EDGE",EDGE,{"disambiguationData":[OSD([sQuery(id+"F4.wireOp",EDGE,"E59.top"),sQuery(id+"F4.wireOp",EDGE,"E59.right")])]})});
            var Q104;
            Q104=makeQuery(id+"F5.boolean.opBoolean","COPY",EDGE,{"derivedFrom":makeQuery(id+"F5.opExtrude","SWEPT_EDGE",EDGE,{"disambiguationData":[OSD([sQuery(id+"F4.wireOp",EDGE,"E58.top"),sQuery(id+"F4.wireOp",EDGE,"E58.right")])]})});
            var Q105;
            Q105=makeQuery(id+"F5.boolean.opBoolean","COPY",EDGE,{"derivedFrom":makeQuery(id+"F5.opExtrude","SWEPT_EDGE",EDGE,{"disambiguationData":[OSD([sQuery(id+"F4.wireOp",EDGE,"E61.top"),sQuery(id+"F4.wireOp",EDGE,"E61.right")])]})});
            var Q106;
            Q106=makeQuery(id+"F5.boolean.opBoolean","COPY",EDGE,{"derivedFrom":makeQuery(id+"F5.opExtrude","SWEPT_EDGE",EDGE,{"disambiguationData":[OSD([sQuery(id+"F4.wireOp",EDGE,"E60.top"),sQuery(id+"F4.wireOp",EDGE,"E60.right")])]})});
            var Q107;
            Q107=makeQuery(id+"F5.boolean.opBoolean","COPY",EDGE,{"derivedFrom":makeQuery(id+"F5.opExtrude","SWEPT_EDGE",EDGE,{"disambiguationData":[OSD([sQuery(id+"F4.wireOp",EDGE,"E57.top"),sQuery(id+"F4.wireOp",EDGE,"E57.right")])]})});
            var Q108;
            Q108=makeQuery(id+"F5.boolean.opBoolean","COPY",EDGE,{"derivedFrom":makeQuery(id+"F5.opExtrude","SWEPT_EDGE",EDGE,{"disambiguationData":[OSD([sQuery(id+"F4.wireOp",EDGE,"E56.top"),sQuery(id+"F4.wireOp",EDGE,"E56.right")])]})});
            var Q109;
            Q109=makeQuery(id+"F5.boolean.opBoolean","COPY",EDGE,{"derivedFrom":makeQuery(id+"F5.opExtrude","SWEPT_EDGE",EDGE,{"disambiguationData":[OSD([sQuery(id+"F4.wireOp",EDGE,"E34.top"),sQuery(id+"F4.wireOp",EDGE,"E34.right")])]})});
            var Q110;
            Q110=makeQuery(id+"F5.boolean.opBoolean","COPY",EDGE,{"derivedFrom":makeQuery(id+"F5.opExtrude","SWEPT_EDGE",EDGE,{"disambiguationData":[OSD([sQuery(id+"F4.wireOp",EDGE,"E33.top"),sQuery(id+"F4.wireOp",EDGE,"E33.right")])]})});
            var Q111;
            Q111=makeQuery(id+"F5.boolean.opBoolean","COPY",EDGE,{"derivedFrom":makeQuery(id+"F5.opExtrude","SWEPT_EDGE",EDGE,{"disambiguationData":[OSD([sQuery(id+"F4.wireOp",EDGE,"E50.top"),sQuery(id+"F4.wireOp",EDGE,"E50.right")])]})});
            var Q112;
            Q112=makeQuery(id+"F5.boolean.opBoolean","COPY",EDGE,{"derivedFrom":makeQuery(id+"F5.opExtrude","SWEPT_EDGE",EDGE,{"disambiguationData":[OSD([sQuery(id+"F4.wireOp",EDGE,"E49.top"),sQuery(id+"F4.wireOp",EDGE,"E49.right")])]})});
            var Q113;
            Q113=makeQuery(id+"F5.boolean.opBoolean","COPY",EDGE,{"derivedFrom":makeQuery(id+"F5.opExtrude","SWEPT_EDGE",EDGE,{"disambiguationData":[OSD([sQuery(id+"F4.wireOp",EDGE,"E48.top"),sQuery(id+"F4.wireOp",EDGE,"E48.right")])]})});
            var Q114;
            Q114=makeQuery(id+"F5.boolean.opBoolean","COPY",EDGE,{"derivedFrom":makeQuery(id+"F5.opExtrude","SWEPT_EDGE",EDGE,{"disambiguationData":[OSD([sQuery(id+"F4.wireOp",EDGE,"E47.top"),sQuery(id+"F4.wireOp",EDGE,"E47.right")])]})});
            var Q115;
            Q115=makeQuery(id+"F5.boolean.opBoolean","COPY",EDGE,{"derivedFrom":makeQuery(id+"F5.opExtrude","SWEPT_EDGE",EDGE,{"disambiguationData":[OSD([sQuery(id+"F4.wireOp",EDGE,"E52.top"),sQuery(id+"F4.wireOp",EDGE,"E52.right")])]})});
            var Q116;
            Q116=makeQuery(id+"F5.boolean.opBoolean","COPY",EDGE,{"derivedFrom":makeQuery(id+"F5.opExtrude","SWEPT_EDGE",EDGE,{"disambiguationData":[OSD([sQuery(id+"F4.wireOp",EDGE,"E53.top"),sQuery(id+"F4.wireOp",EDGE,"E53.right")])]})});
            var Q117;
            Q117=makeQuery(id+"F5.boolean.opBoolean","COPY",EDGE,{"derivedFrom":makeQuery(id+"F5.opExtrude","SWEPT_EDGE",EDGE,{"disambiguationData":[OSD([sQuery(id+"F4.wireOp",EDGE,"E54.top"),sQuery(id+"F4.wireOp",EDGE,"E54.right")])]})});
            var Q118;
            Q118=makeQuery(id+"F5.boolean.opBoolean","COPY",EDGE,{"derivedFrom":makeQuery(id+"F5.opExtrude","SWEPT_EDGE",EDGE,{"disambiguationData":[OSD([sQuery(id+"F4.wireOp",EDGE,"E55.top"),sQuery(id+"F4.wireOp",EDGE,"E55.right")])]})});
            var Q119;
            Q119=makeQuery(id+"F5.boolean.opBoolean","COPY",EDGE,{"derivedFrom":makeQuery(id+"F5.opExtrude","SWEPT_EDGE",EDGE,{"disambiguationData":[OSD([sQuery(id+"F4.wireOp",EDGE,"E49.bottom"),sQuery(id+"F4.wireOp",EDGE,"E49.right")])]})});
            fillet(context, id + "F6", {"entities" : qUnion([Q0, Q1, Q2, Q3, Q4, Q5, Q6, Q7, Q8, Q9, Q10, Q11, Q12, Q13, Q14, Q15, Q16, Q17, Q18, Q19, Q20, Q21, Q22, Q23, Q24, Q25, Q26, Q27, Q28, Q29, Q30, Q31, Q32, Q33, Q34, Q35, Q36, Q37, Q38, Q39, Q40, Q41, Q42, Q43, Q44, Q45, Q46, Q47, Q48, Q49, Q50, Q51, Q52, Q53, Q54, Q55, Q56, Q57, Q58, Q59, Q60, Q61, Q62, Q63, Q64, Q65, Q66, Q67, Q68, Q69, Q70, Q71, Q72, Q73, Q74, Q75, Q76, Q77, Q78, Q79, Q80, Q81, Q82, Q83, Q84, Q85, Q86, Q87, Q88, Q89, Q90, Q91, Q92, Q93, Q94, Q95, Q96, Q97, Q98, Q99, Q100, Q101, Q102, Q103, Q104, Q105, Q106, Q107, Q108, Q109, Q110, Q111, Q112, Q113, Q114, Q115, Q116, Q117, Q118, Q119]), "radius" : 1.2 * mm, "tangentPropagation" : true, "allowEdgeOverflow" : false});
        }
    });
